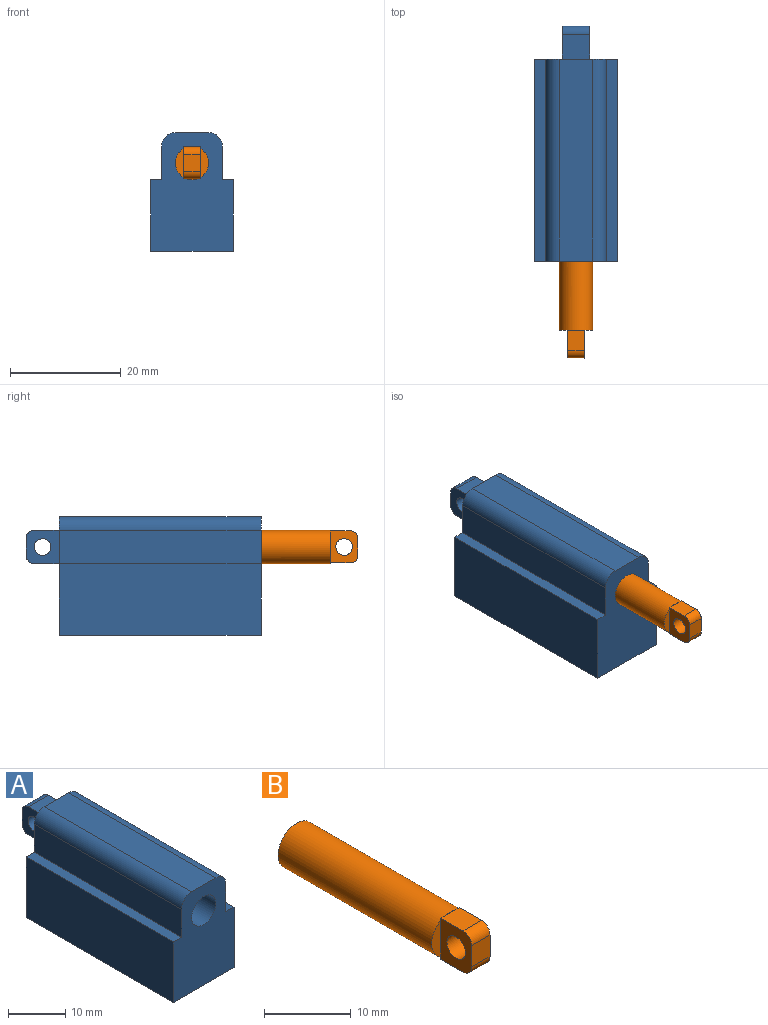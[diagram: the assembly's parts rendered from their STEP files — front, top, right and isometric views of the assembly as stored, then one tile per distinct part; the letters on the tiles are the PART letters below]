
ASSEMBLY  parts=2 mates=1
PART A: 22 faces, bbox 15x42.5x21.5 mm
  f0: plane 21.5x15mm, normal (0,1,0), area 255.8mm2, adj f1,f2,f3,f4,f5,f6,f7,f8
  f1: plane 36.5x6mm, normal (-1,0,0), area 219mm2, adj f0,f2,f10,f12
  f2: plane 36.5x2mm, normal (0,0,1), area 73mm2, adj f0,f1,f3,f12
  f3: plane 36.5x13mm, normal (-1,0,0), area 474.5mm2, adj f0,f2,f4,f12
  f4: plane 36.5x15mm, normal (0,0,-1), area 547.5mm2, adj f0,f3,f5,f12
  f5: plane 36.5x13mm, normal (1,0,0), area 474.5mm2, adj f0,f4,f6,f12
  f6: plane 36.5x2mm, normal (0,0,1), area 73mm2, adj f0,f5,f7,f12
  f7: plane 36.5x6mm, normal (1,0,0), area 219mm2, adj f0,f6,f8,f12
  f8: cylinder r=2.5mm len=36.5mm, axis (0,1,0), area 143.3mm2, adj f0,f7,f9,f12
  f9: plane 36.5x6mm, normal (0,0,1), area 219mm2, adj f0,f8,f10,f12
  f10: cylinder r=2.5mm len=36.5mm, axis (0,1,0), area 143.3mm2, adj f0,f1,f9,f12
  f11: cylinder r=3mm len=26.5mm, axis (0,1,0), area 499.5mm2, adj f12,f13
  f12: plane 21.5x15mm, normal (0,-1,0), area 257.5mm2, adj f1,f2,f3,f4,f5,f6,f7,f8
  f13: plane 6x6mm, normal (0,-1,0), area 28.3mm2, adj f11
  f14: plane 5x4.5mm, normal (0,0,1), area 22.5mm2, adj f0,f19,f20,f21
  f15: plane 5x4.5mm, normal (0,0,-1), area 22.5mm2, adj f0,f16,f20,f21
  f16: cylinder r=1.5mm len=5mm, axis (-1,0,0), area 11.8mm2, adj f15,f17,f20,f21
  f17: plane 5x3mm, normal (0,1,0), area 15mm2, adj f16,f19,f20,f21
  f18: cylinder r=1.5mm len=5mm, axis (-1,0,0), area 47.1mm2, adj f20,f21
  f19: cylinder r=1.5mm len=5mm, axis (-1,0,0), area 11.8mm2, adj f14,f17,f20,f21
  f20: plane 6x6mm, normal (1,0,0), area 28mm2, adj f0,f14,f15,f16,f17,f18,f19
  f21: plane 6x6mm, normal (-1,0,0), area 28mm2, adj f0,f14,f15,f16,f17,f18,f19
PART B: 18 faces, bbox 6x30x6 mm
  f0: plane 0.73x0.3mm, normal (0,1,0), area 0.1mm2, adj f3,f10,f15
  f1: plane 0.73x0.3mm, normal (0,1,0), area 0.1mm2, adj f5,f10,f15
  f2: plane 0.73x0.3mm, normal (0,1,0), area 0.1mm2, adj f5,f11,f15
  f3: plane 3.6x3mm, normal (0,0,-1), area 10.8mm2, adj f0,f4,f9,f10,f11,f14
  f4: plane 0.73x0.3mm, normal (0,1,0), area 0.1mm2, adj f3,f11,f15
  f5: plane 3.6x3mm, normal (0,0,1), area 10.8mm2, adj f1,f2,f6,f10,f11,f13
  f6: cylinder r=1.4mm len=3mm, axis (-1,0,0), area 6.6mm2, adj f5,f7,f10,f11
  f7: plane 3x3mm, normal (0,-1,0), area 9mm2, adj f6,f9,f10,f11
  f8: cylinder r=1.5mm len=3mm, axis (-1,0,0), area 28.3mm2, adj f10,f11
  f9: cylinder r=1.4mm len=3mm, axis (-1,0,0), area 6.6mm2, adj f3,f7,f10,f11
  f10: plane 5.8x5mm, normal (1,0,0), area 21.1mm2, adj f0,f1,f3,f5,f6,f7,f8,f9
  f11: plane 5.8x5mm, normal (-1,0,0), area 21.1mm2, adj f2,f3,f4,f5,f6,f7,f8,f9
  f12: plane 5.2x1.5mm, normal (0,-1,0), area 5.5mm2, adj f11,f15
  f13: plane 1.54x0.1mm, normal (0,-1,0), area 0.1mm2, adj f5,f15
  f14: plane 1.54x0.1mm, normal (0,-1,0), area 0.1mm2, adj f3,f15
  f15: cylinder r=3mm len=25mm, axis (0,-1,0), area 471.2mm2, adj f0,f1,f2,f4,f12,f13,f14,f16
  f16: plane 6x6mm, normal (0,1,0), area 28.3mm2, adj f15
  f17: plane 5.2x1.5mm, normal (0,-1,0), area 5.5mm2, adj f10,f15
PLACE A t=(-2.79,22.53,1.44)mm
PLACE B t=(-2.79,10.03,1.44)mm
MATE slider A.f11 <-> B.f15  axis (0,-1,0) through (-2.79,-13.97,1.44)mm
